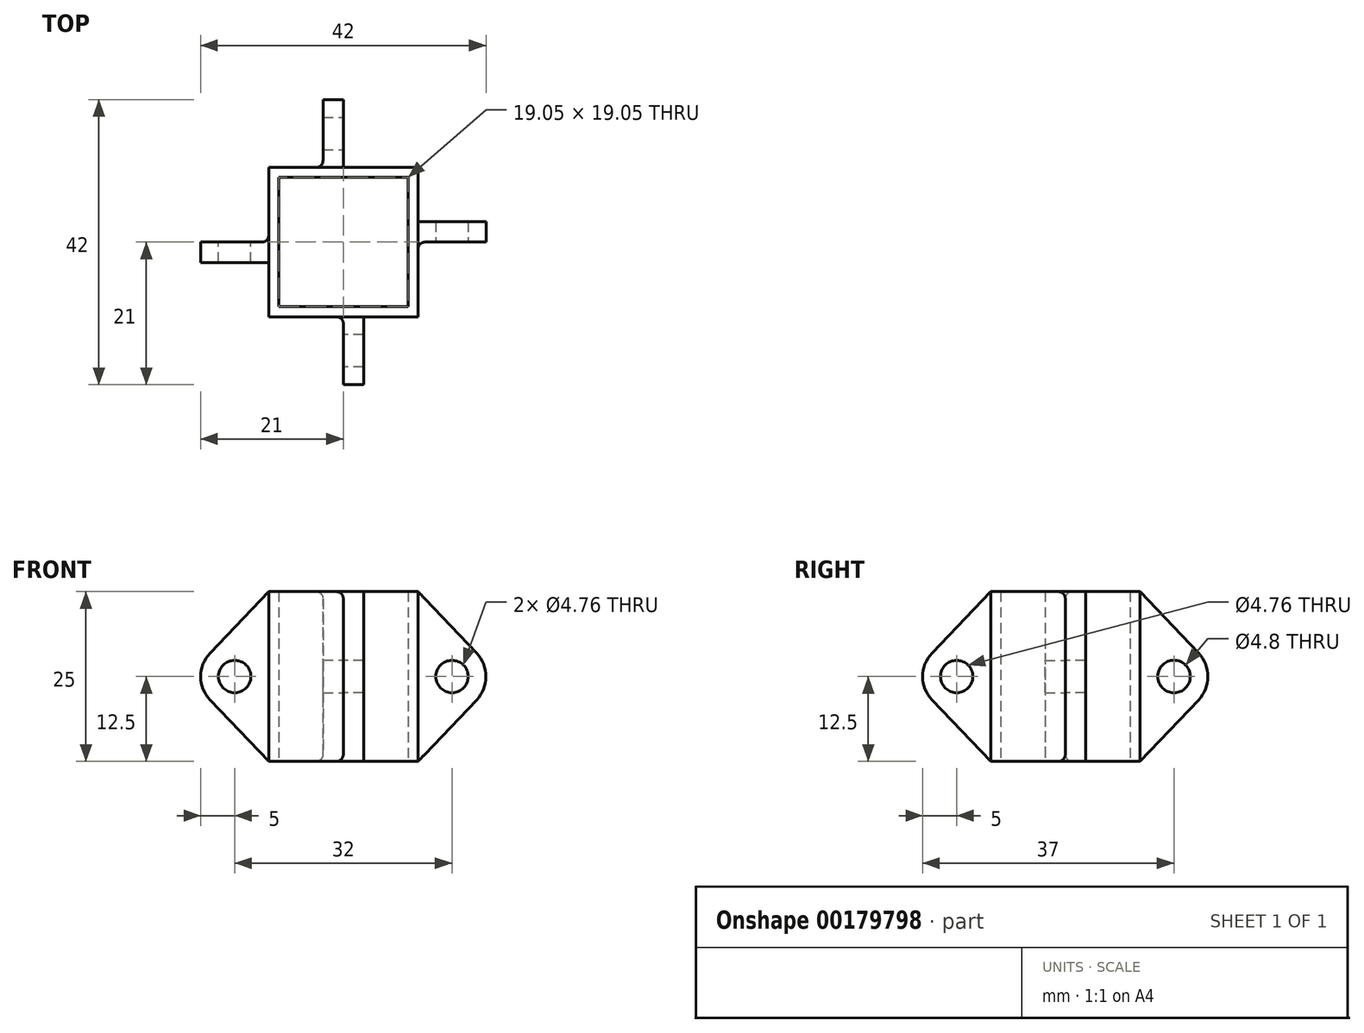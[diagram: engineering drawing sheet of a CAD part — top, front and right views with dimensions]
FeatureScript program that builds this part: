
annotation { "Feature Type Name" : "Feature", "Feature Type Description" : "" }
export const myFeature = defineFeature(function(context is Context, id is Id, definition is map)
    precondition{}
    {
        {
            var Q0;
            Q0=qCreatedBy(makeId("Top.planeOp"),FACE);
            var sketch = newSketch(context, id + "F0", { "sketchPlane" : qUnion([Q0])});
            skLineSegment(sketch, "E0.bottom", {"start": v(-9.53, 9.53) * mm, "end": v(9.53, 9.52) * mm});
            skLineSegment(sketch, "E0.top", {"start": v(-9.53, -9.52) * mm, "end": v(9.53, -9.53) * mm});
            skLineSegment(sketch, "E0.left", {"start": v(-9.52, 9.52) * mm, "end": v(-9.53, -9.52) * mm});
            skLineSegment(sketch, "E0.right", {"start": v(9.53, 9.52) * mm, "end": v(9.52, -9.52) * mm});
            skLineSegment(sketch, "E1.bottom", {"start": v(-11, 11) * mm, "end": v(11, 11) * mm});
            skLineSegment(sketch, "E1.top", {"start": v(-11, -11) * mm, "end": v(11, -11) * mm});
            skLineSegment(sketch, "E1.left", {"start": v(-11, 11) * mm, "end": v(-11, -11) * mm});
            skLineSegment(sketch, "E1.right", {"start": v(11, 11) * mm, "end": v(11, -11) * mm});
            skSolve(sketch);
        }
        {
            var Q0;
            Q0 = qSketchRegion(id + "F0", true);
            extrude(context, id + "F1", {"entities" : qUnion([Q0]), "endBound" : BoundingType.SYMMETRIC, "depth" : 25 * mm});
        }
        {
            var Q0;
            Q0=qCreatedBy(makeId("Front.planeOp"),FACE);
            var sketch = newSketch(context, id + "F2", { "sketchPlane" : qUnion([Q0])});
            skCircle(sketch, "E2", {"center": v(-16, 0) * mm, "radius": 2.38 * mm});
            skLineSegment(sketch, "E3", {"start": v(-11, 12.5) * mm, "end": v(-19.62, 3.45) * mm});
            skLineSegment(sketch, "E4", {"start": v(-19.62, -3.45) * mm, "end": v(-11, -12.5) * mm});
            skArc(sketch, "E5", {"start": v(-19.62, 3.45) * mm, "mid": v(-21, 0) * mm, "end": v(-19.62, -3.45) * mm});
            skLineSegment(sketch, "E6", {"start": v(-11, 12.5) * mm, "end": v(-11, -12.5) * mm});
            skSolve(sketch);
        }
        {
            var Q0;
            Q0 = qSketchRegion(id + "F2", true);
            extrude(context, id + "F3", {"entities" : qUnion([Q0]), "operationType" : NewBodyOperationType.ADD, "depth" : 3 * mm});
        }
        {
            var Q0;
            Q0=qCreatedBy(makeId("Right.planeOp"),FACE);
            var sketch = newSketch(context, id + "F4", { "sketchPlane" : qUnion([Q0])});
            skCircle(sketch, "E7", {"center": v(-16, 0) * mm, "radius": 2.38 * mm});
            skLineSegment(sketch, "E8", {"start": v(-19.62, 3.45) * mm, "end": v(-11, 12.5) * mm});
            skLineSegment(sketch, "E9.MirrorCS", {"start": v(-19.62, -3.45) * mm, "end": v(-11, -12.5) * mm});
            skLineSegment(sketch, "E10", {"start": v(-11, 12.5) * mm, "end": v(-11, -12.5) * mm});
            skArc(sketch, "E11", {"start": v(-19.62, 3.45) * mm, "mid": v(-21, 0) * mm, "end": v(-19.62, -3.45) * mm});
            skSolve(sketch);
        }
        {
            var Q0;
            Q0 = qSketchRegion(id + "F4", true);
            extrude(context, id + "F5", {"entities" : qUnion([Q0]), "operationType" : NewBodyOperationType.ADD, "depth" : 3 * mm});
        }
        {
            var Q0;
            Q0=qCreatedBy(makeId("Front.planeOp"),FACE);
            var sketch = newSketch(context, id + "F6", { "sketchPlane" : qUnion([Q0])});
            skCircle(sketch, "E12", {"center": v(16, 0) * mm, "radius": 2.38 * mm});
            skLineSegment(sketch, "E13", {"start": v(19.62, -3.45) * mm, "end": v(11, -12.5) * mm});
            skLineSegment(sketch, "E14", {"start": v(11, 12.5) * mm, "end": v(19.62, 3.45) * mm});
            skLineSegment(sketch, "E15", {"start": v(11, -12.5) * mm, "end": v(11, 12.5) * mm});
            skArc(sketch, "E16", {"start": v(19.62, -3.45) * mm, "mid": v(21, 0) * mm, "end": v(19.62, 3.45) * mm});
            skSolve(sketch);
        }
        {
            var Q0;
            Q0 = qSketchRegion(id + "F6", true);
            extrude(context, id + "F7", {"entities" : qUnion([Q0]), "operationType" : NewBodyOperationType.ADD, "oppositeDirection" : true, "depth" : 3 * mm});
        }
        {
            var Q0;
            Q0=qCreatedBy(makeId("Right.planeOp"),FACE);
            var sketch = newSketch(context, id + "F8", { "sketchPlane" : qUnion([Q0])});
            skCircle(sketch, "E17", {"center": v(16, 0) * mm, "radius": 2.4 * mm});
            skLineSegment(sketch, "E18", {"start": v(19.62, 3.45) * mm, "end": v(11, 12.5) * mm});
            skLineSegment(sketch, "E19", {"start": v(11, 12.5) * mm, "end": v(11, -12.5) * mm});
            skLineSegment(sketch, "E20", {"start": v(11, -12.5) * mm, "end": v(19.62, -3.45) * mm});
            skArc(sketch, "E21", {"start": v(19.62, -3.45) * mm, "mid": v(21, 0) * mm, "end": v(19.62, 3.45) * mm});
            skSolve(sketch);
        }
        {
            var Q0;
            Q0 = qSketchRegion(id + "F8", true);
            extrude(context, id + "F9", {"entities" : qUnion([Q0]), "operationType" : NewBodyOperationType.ADD, "oppositeDirection" : true, "depth" : 3 * mm});
        }
        {
            var Q0;
            Q0=makeQuery(id+"F3.opExtrude","CAP_EDGE",EDGE,{"disambiguationData":[OSD([sQuery(id+"F2.wireOp",EDGE,"E6")])],"isStart":false});
            var Q1;
            Q1=makeQuery(id+"F5.opExtrude","CAP_EDGE",EDGE,{"disambiguationData":[OSD([sQuery(id+"F4.wireOp",EDGE,"E10")])],"isStart":true});
            var Q2;
            Q2=makeQuery(id+"F5.opExtrude","CAP_EDGE",EDGE,{"disambiguationData":[OSD([sQuery(id+"F4.wireOp",EDGE,"E10")])],"isStart":false});
            var Q3;
            Q3=makeQuery(id+"F3.opExtrude","CAP_EDGE",EDGE,{"disambiguationData":[OSD([sQuery(id+"F2.wireOp",EDGE,"5e426696-2d0d-4448-9194-7e160c71353e2.MirrorCS")])],"isStart":false});
            var Q4;
            Q4=makeQuery(id+"F3.opExtrude","CAP_EDGE",EDGE,{"disambiguationData":[OSD([sQuery(id+"F2.wireOp",EDGE,"5e426696-2d0d-4448-9194-7e160c71353e2.MirrorCS")])],"isStart":true});
            var Q5;
            Q5=makeQuery(id+"F5.opExtrude","CAP_EDGE",EDGE,{"disambiguationData":[OSD([sQuery(id+"F4.wireOp",EDGE,"1f8986f2-1053-424e-8057-c49cb6aa39cc2.MirrorCS")])],"isStart":false});
            var Q6;
            Q6=makeQuery(id+"F3.opExtrude","CAP_EDGE",EDGE,{"disambiguationData":[OSD([sQuery(id+"F2.wireOp",EDGE,"E6")])],"isStart":true});
            var Q7;
            Q7=makeQuery(id+"F5.opExtrude","CAP_EDGE",EDGE,{"disambiguationData":[OSD([sQuery(id+"F4.wireOp",EDGE,"1f8986f2-1053-424e-8057-c49cb6aa39cc2.MirrorCS")])],"isStart":true});
            var Q8;
            Q8=makeQuery(id+"F7.opExtrude","CAP_EDGE",EDGE,{"disambiguationData":[OSD([sQuery(id+"F6.wireOp",EDGE,"E15")])],"isStart":true});
            var Q9;
            Q9=makeQuery(id+"F7.opExtrude","CAP_EDGE",EDGE,{"disambiguationData":[OSD([sQuery(id+"F6.wireOp",EDGE,"E15")])],"isStart":false});
            var Q10;
            Q10=makeQuery(id+"F9.opExtrude","CAP_EDGE",EDGE,{"disambiguationData":[OSD([sQuery(id+"F8.wireOp",EDGE,"E19")])],"isStart":true});
            var Q11;
            Q11=makeQuery(id+"F9.opExtrude","CAP_EDGE",EDGE,{"disambiguationData":[OSD([sQuery(id+"F8.wireOp",EDGE,"E19")])],"isStart":false});
            fillet(context, id + "F10", {"entities" : qUnion([Q0, Q1, Q2, Q3, Q4, Q5, Q6, Q7, Q8, Q9, Q10, Q11]), "radius" : 1 * mm, "tangentPropagation" : true, "allowEdgeOverflow" : false});
        }
    });
